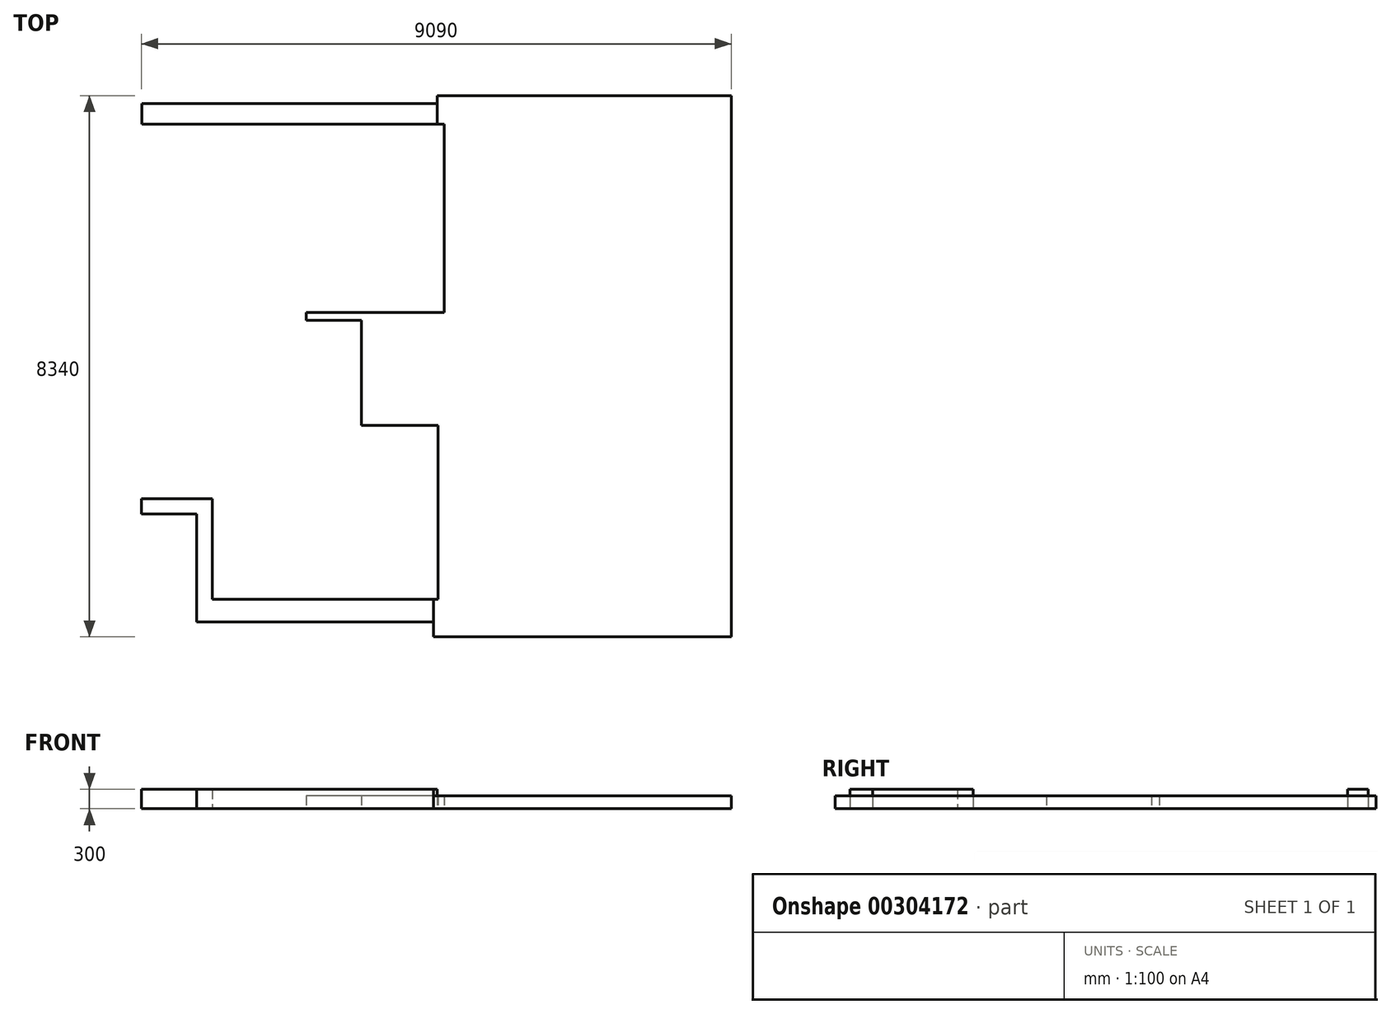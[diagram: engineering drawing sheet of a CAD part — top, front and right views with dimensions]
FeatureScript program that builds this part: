
annotation { "Feature Type Name" : "Feature", "Feature Type Description" : "" }
export const myFeature = defineFeature(function(context is Context, id is Id, definition is map)
    precondition{}
    {
        {
            var Q0;
            Q0=qCreatedBy(makeId("Top.planeOp"),FACE);
            var sketch = newSketch(context, id + "F0", { "sketchPlane" : qUnion([Q0])});
            skLineSegment(sketch, "E0", {"start": v(-4088.87, -3110) * mm, "end": v(-3238.87, -3110) * mm});
            skLineSegment(sketch, "E1", {"start": v(-3238.87, -3110) * mm, "end": v(-3238.87, -4770) * mm});
            skLineSegment(sketch, "E2", {"start": v(-3238.87, -4770) * mm, "end": v(411.13, -4770) * mm});
            skLineSegment(sketch, "E3", {"start": v(411.13, -4770) * mm, "end": v(411.13, -5000) * mm});
            skLineSegment(sketch, "E4", {"start": v(411.13, -5000) * mm, "end": v(5001.13, -5000) * mm});
            skLineSegment(sketch, "E5", {"start": v(5001.13, -5000) * mm, "end": v(5001.13, 3340) * mm});
            skLineSegment(sketch, "E6", {"start": v(-4088.87, -2870) * mm, "end": v(-4088.87, -3110) * mm});
            skLineSegment(sketch, "E7.bottom", {"start": v(-2998.87, -4420) * mm, "end": v(481.13, -4420) * mm});
            skLineSegment(sketch, "E7.right", {"start": v(481.13, -4420) * mm, "end": v(481.13, -1740) * mm});
            skLineSegment(sketch, "E8", {"start": v(481.13, -1740) * mm, "end": v(-698.87, -1740) * mm});
            skLineSegment(sketch, "E9", {"start": v(5001.13, 3340) * mm, "end": v(575.26, 3340) * mm});
            skLineSegment(sketch, "E10", {"start": v(-2998.87, -4420) * mm, "end": v(-2998.87, -2870) * mm});
            skLineSegment(sketch, "E11", {"start": v(-2998.87, -2870) * mm, "end": v(-4088.87, -2870) * mm});
            skLineSegment(sketch, "E12", {"start": v(575.26, 0) * mm, "end": v(-1548.87, 0) * mm});
            skLineSegment(sketch, "E13", {"start": v(-698.87, -1740) * mm, "end": v(-698.87, -124.04) * mm});
            skLineSegment(sketch, "E14", {"start": v(-698.87, -124.04) * mm, "end": v(-1548.87, -124.04) * mm});
            skLineSegment(sketch, "E15", {"start": v(-1548.87, -124.04) * mm, "end": v(-1548.87, 0) * mm});
            skLineSegment(sketch, "E16", {"start": v(575.26, 3340) * mm, "end": v(471.13, 3340) * mm});
            skLineSegment(sketch, "E17", {"start": v(471.13, 3340) * mm, "end": v(471.13, 3220) * mm});
            skLineSegment(sketch, "E18", {"start": v(471.13, 3220) * mm, "end": v(-4083.87, 3220) * mm});
            skLineSegment(sketch, "E19", {"start": v(-4083.87, 3220) * mm, "end": v(-4083.87, 2900) * mm});
            skLineSegment(sketch, "E20", {"start": v(-4083.87, 2900) * mm, "end": v(575.26, 2900) * mm});
            skLineSegment(sketch, "E21", {"start": v(575.26, 2900) * mm, "end": v(575.26, 0) * mm});
            skSolve(sketch);
        }
        {
            var Q0;
            Q0=makeQuery(id+"F0.imprint","IMPRINT",FACE,{"disambiguationData":[TD([[makeQuery(id+"F0.imprint","IMPRINT",EDGE,{"derivedFrom":sQuery(id+"F0.wireOp",EDGE,"E0")}),1.0]])]});
            extrude(context, id + "F1", {"entities" : qUnion([Q0]), "depth" : 200 * mm});
        }
        {
            var Q0;
            Q0=makeQuery(id+"F1.opExtrude","CAP_FACE",FACE,{"disambiguationData":[OSD([sQuery(id+"F0.wireOp",EDGE,"E0"),sQuery(id+"F0.wireOp",EDGE,"E1"),sQuery(id+"F0.wireOp",EDGE,"E2"),sQuery(id+"F0.wireOp",EDGE,"E3"),sQuery(id+"F0.wireOp",EDGE,"E4"),sQuery(id+"F0.wireOp",EDGE,"E5"),sQuery(id+"F0.wireOp",EDGE,"E6"),sQuery(id+"F0.wireOp",EDGE,"E7.bottom"),sQuery(id+"F0.wireOp",EDGE,"E7.right"),sQuery(id+"F0.wireOp",EDGE,"E8"),sQuery(id+"F0.wireOp",EDGE,"E9"),sQuery(id+"F0.wireOp",EDGE,"E10"),sQuery(id+"F0.wireOp",EDGE,"E11"),sQuery(id+"F0.wireOp",EDGE,"E12"),sQuery(id+"F0.wireOp",EDGE,"E13"),sQuery(id+"F0.wireOp",EDGE,"E14"),sQuery(id+"F0.wireOp",EDGE,"E15"),sQuery(id+"F0.wireOp",EDGE,"E16"),sQuery(id+"F0.wireOp",EDGE,"E17"),sQuery(id+"F0.wireOp",EDGE,"E18"),sQuery(id+"F0.wireOp",EDGE,"E19"),sQuery(id+"F0.wireOp",EDGE,"E20"),sQuery(id+"F0.wireOp",EDGE,"E21")])],"isStart":false});
            var sketch = newSketch(context, id + "F2", { "sketchPlane" : qUnion([Q0])});
            skLineSegment(sketch, "E22", {"start": v(-4088.87, -2870) * mm, "end": v(-2998.87, -2870) * mm});
            skLineSegment(sketch, "E23", {"start": v(-2998.87, -2870) * mm, "end": v(-2998.87, -4420) * mm});
            skLineSegment(sketch, "E24", {"start": v(-2998.87, -4420) * mm, "end": v(411.13, -4420) * mm});
            skLineSegment(sketch, "E25", {"start": v(411.13, -4420) * mm, "end": v(411.13, -4770) * mm});
            skLineSegment(sketch, "E26", {"start": v(411.13, -4770) * mm, "end": v(-3238.87, -4770) * mm});
            skLineSegment(sketch, "E27", {"start": v(-3238.87, -4770) * mm, "end": v(-3238.87, -3110) * mm});
            skLineSegment(sketch, "E28", {"start": v(-3238.87, -3110) * mm, "end": v(-4088.87, -3110) * mm});
            skLineSegment(sketch, "E29", {"start": v(-4088.87, -3110) * mm, "end": v(-4088.87, -2870) * mm});
            skLineSegment(sketch, "E30", {"start": v(-4083.87, 2900) * mm, "end": v(-4083.87, 3220) * mm});
            skLineSegment(sketch, "E31", {"start": v(-4083.87, 3220) * mm, "end": v(471.13, 3220) * mm});
            skLineSegment(sketch, "E32", {"start": v(471.13, 3220) * mm, "end": v(471.13, 2900) * mm});
            skLineSegment(sketch, "E33", {"start": v(471.13, 2900) * mm, "end": v(-4083.87, 2900) * mm});
            skSolve(sketch);
        }
        {
            var Q0;
            Q0=makeQuery(id+"F2.imprint","IMPRINT",FACE,{"disambiguationData":[TD([[makeQuery(id+"F2.imprint","IMPRINT",EDGE,{"derivedFrom":sQuery(id+"F2.wireOp",EDGE,"E22")}),1.0]])]});
            var Q1;
            Q1=makeQuery(id+"F2.imprint","IMPRINT",FACE,{"disambiguationData":[TD([[makeQuery(id+"F2.imprint","IMPRINT",EDGE,{"derivedFrom":sQuery(id+"F2.wireOp",EDGE,"E30")}),1.0]])]});
            extrude(context, id + "F3", {"entities" : qUnion([Q0, Q1]), "operationType" : NewBodyOperationType.ADD, "depth" : 100 * mm});
        }
    });
